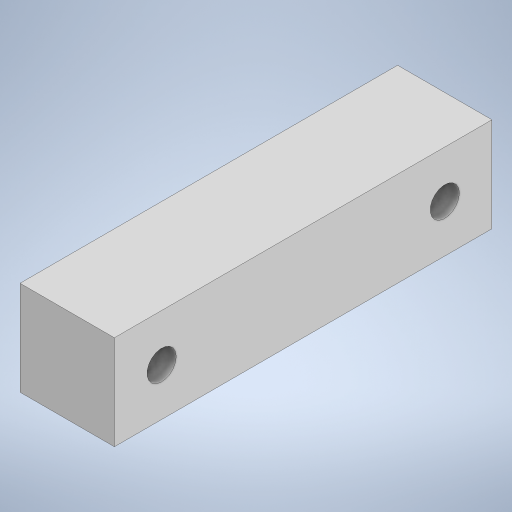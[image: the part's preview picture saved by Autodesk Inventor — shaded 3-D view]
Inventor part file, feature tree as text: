
AUTODESK INVENTOR PART (.ipt)
format: ipt  version: 2023 (Build 270158000, 158)  size: 199,680 bytes
history: native  units: mm
features: sketch x2, other x1, extrude x1, hole x1
ambient origin geometry x8: Origin, YZ Plane, XZ Plane, XY Plane, X Axis, Y Axis, Z Axis, Center Point
bodies: Body1 (feature_tree)
feature tree (5):
  other  "ソリッド1"
  extrude  "押し出し1"  Depth=10.0mm
  hole  "穴1"  [1 undecoded]
  sketch  "スケッチ1"
  sketch  "スケッチ2"
note: 1 required parameter value undecoded (feature->parameter linkage not recoverable at this tier; creation-order binding heuristic only, values carry confidence <= 0.55)
